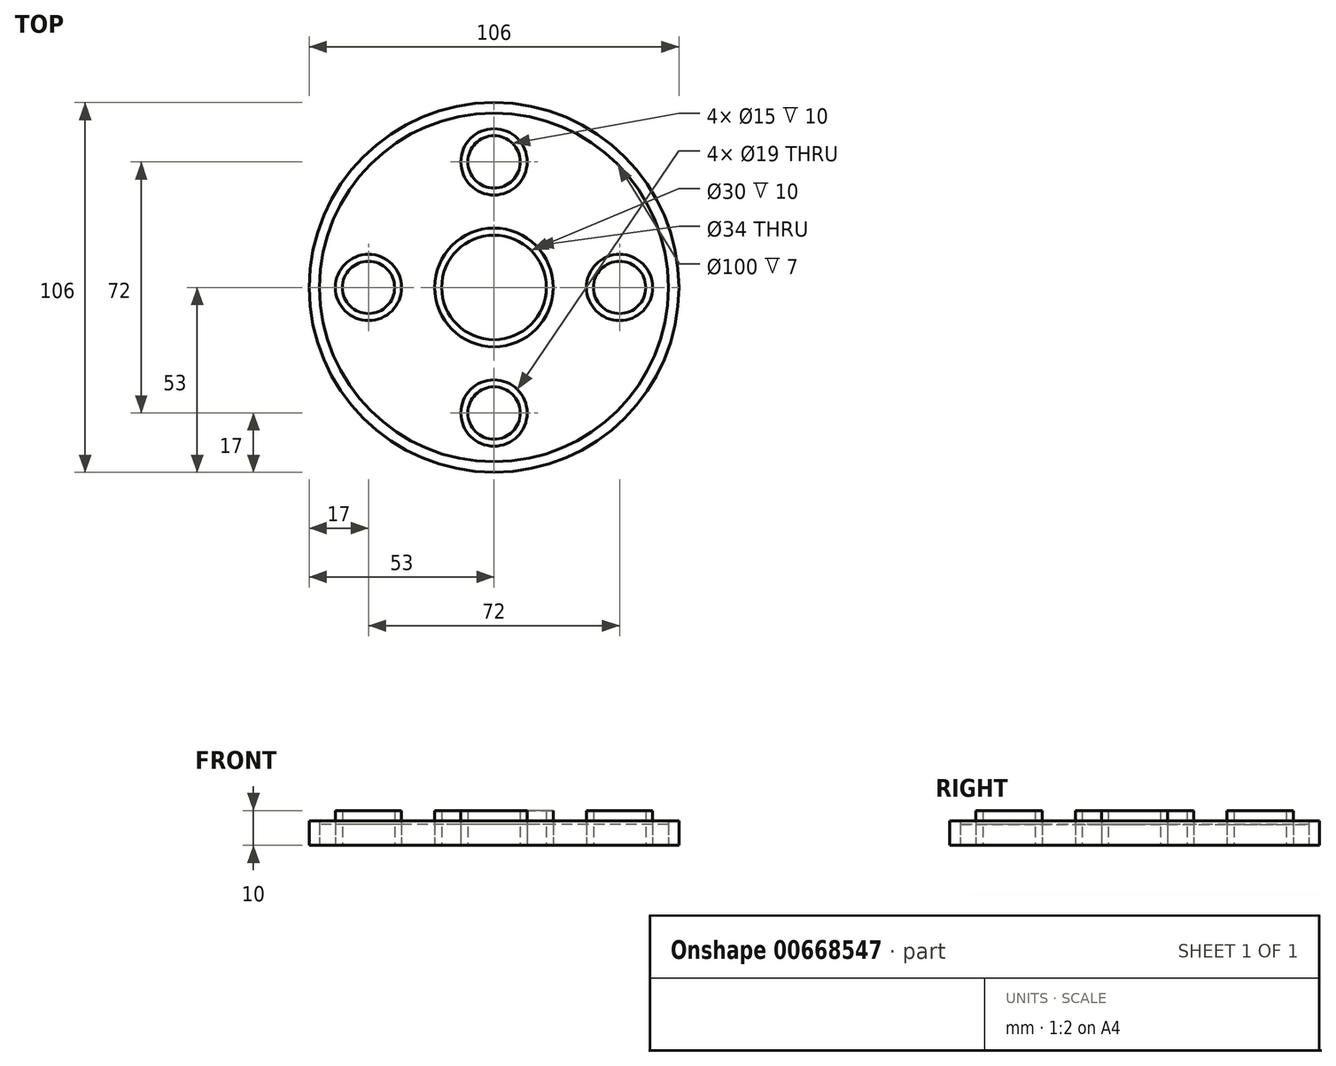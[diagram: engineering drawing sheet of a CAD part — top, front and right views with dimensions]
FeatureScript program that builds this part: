
annotation { "Feature Type Name" : "Feature", "Feature Type Description" : "" }
export const myFeature = defineFeature(function(context is Context, id is Id, definition is map)
    precondition{}
    {
        {
            var Q0;
            Q0=qCreatedBy(makeId("Top.planeOp"),FACE);
            var sketch = newSketch(context, id + "F0", { "sketchPlane" : qUnion([Q0])});
            skCircle(sketch, "E0", {"center": v(0, 0) * mm, "radius": 50 * mm});
            skCircle(sketch, "E1", {"center": v(0, 0) * mm, "radius": 53 * mm});
            skCircle(sketch, "E2", {"center": v(0, 0) * mm, "radius": 15 * mm});
            skCircle(sketch, "E3", {"center": v(0, 0) * mm, "radius": 17 * mm});
            skCircle(sketch, "E4", {"center": v(-36, 0) * mm, "radius": 7.5 * mm});
            skCircle(sketch, "E5", {"center": v(-36, 0) * mm, "radius": 9.5 * mm});
            skCircle(sketch, "E6.1.0", {"center": v(0, -36) * mm, "radius": 9.5 * mm});
            skCircle(sketch, "E6.1.1", {"center": v(0, -36) * mm, "radius": 7.5 * mm});
            skCircle(sketch, "E6.2.0", {"center": v(36, 0) * mm, "radius": 9.5 * mm});
            skCircle(sketch, "E6.2.1", {"center": v(36, 0) * mm, "radius": 7.5 * mm});
            skCircle(sketch, "E6.3.0", {"center": v(0, 36) * mm, "radius": 9.5 * mm});
            skCircle(sketch, "E6.3.1", {"center": v(0, 36) * mm, "radius": 7.5 * mm});
            skSolve(sketch);
        }
        {
            var Q0;
            Q0=makeQuery(id+"F0.imprint","IMPRINT",FACE,{"disambiguationData":[TD([[makeQuery(id+"F0.imprint","IMPRINT",EDGE,{"derivedFrom":sQuery(id+"F0.wireOp",EDGE,"E0")}),-1.0]])]});
            extrude(context, id + "F1", {"entities" : qUnion([Q0]), "depth" : 7 * mm, "offsetDistance" : 25 * mm});
        }
        {
            var Q0;
            Q0=makeQuery(id+"F0.imprint","IMPRINT",FACE,{"disambiguationData":[TD([[makeQuery(id+"F0.imprint","IMPRINT",EDGE,{"derivedFrom":sQuery(id+"F0.wireOp",EDGE,"E6.2.0")}),1.0]])]});
            var Q1;
            Q1=makeQuery(id+"F0.imprint","IMPRINT",FACE,{"disambiguationData":[TD([[makeQuery(id+"F0.imprint","IMPRINT",EDGE,{"derivedFrom":sQuery(id+"F0.wireOp",EDGE,"E4")}),-1.0]])]});
            var Q2;
            Q2=makeQuery(id+"F0.imprint","IMPRINT",FACE,{"disambiguationData":[TD([[makeQuery(id+"F0.imprint","IMPRINT",EDGE,{"derivedFrom":sQuery(id+"F0.wireOp",EDGE,"E6.1.0")}),1.0]])]});
            var Q3;
            Q3=makeQuery(id+"F0.imprint","IMPRINT",FACE,{"disambiguationData":[TD([[makeQuery(id+"F0.imprint","IMPRINT",EDGE,{"derivedFrom":sQuery(id+"F0.wireOp",EDGE,"E6.3.0")}),1.0]])]});
            var Q4;
            Q4=makeQuery(id+"F0.imprint","IMPRINT",FACE,{"disambiguationData":[TD([[makeQuery(id+"F0.imprint","IMPRINT",EDGE,{"derivedFrom":sQuery(id+"F0.wireOp",EDGE,"E2")}),-1.0]])]});
            extrude(context, id + "F2", {"entities" : qUnion([Q0, Q1, Q2, Q3, Q4]), "depth" : 10 * mm, "offsetDistance" : 25 * mm});
        }
        {
            var Q0;
            Q0=makeQuery(id+"F0.imprint","IMPRINT",FACE,{"disambiguationData":[TD([[makeQuery(id+"F0.imprint","IMPRINT",EDGE,{"derivedFrom":sQuery(id+"F0.wireOp",EDGE,"E0")}),1.0]])]});
            extrude(context, id + "F3", {"entities" : qUnion([Q0]), "depth" : 6 * mm, "offsetDistance" : 25 * mm});
        }
    });
